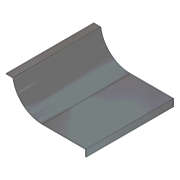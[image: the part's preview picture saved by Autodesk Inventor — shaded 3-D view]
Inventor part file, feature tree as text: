
AUTODESK INVENTOR PART (.ipt)
format: ipt  version: 2012 (Build 160160000, 160)  size: 92,160 bytes
history: native  units: in
note: dims shown in document units (in); Inventor stores cm internally (conversion verified against a paired STEP export)
features: extrude x1, sketch x1
ambient origin geometry x8: Origin, YZ Plane, XZ Plane, XY Plane, X Axis, Y Axis, Z Axis, Center Point
bodies: Solid1 (feature_tree)
feature tree (2):
  extrude  "Extrusion1"  Depth=0.125in
  sketch  "Sketch1"  dims[d0=1.0in d2=0.125in d3=0.125in d4=0.5in d5=4.0in d6=6.0in d7=0.125in d8=1.0in d9=12.0in d10=0.0in]
